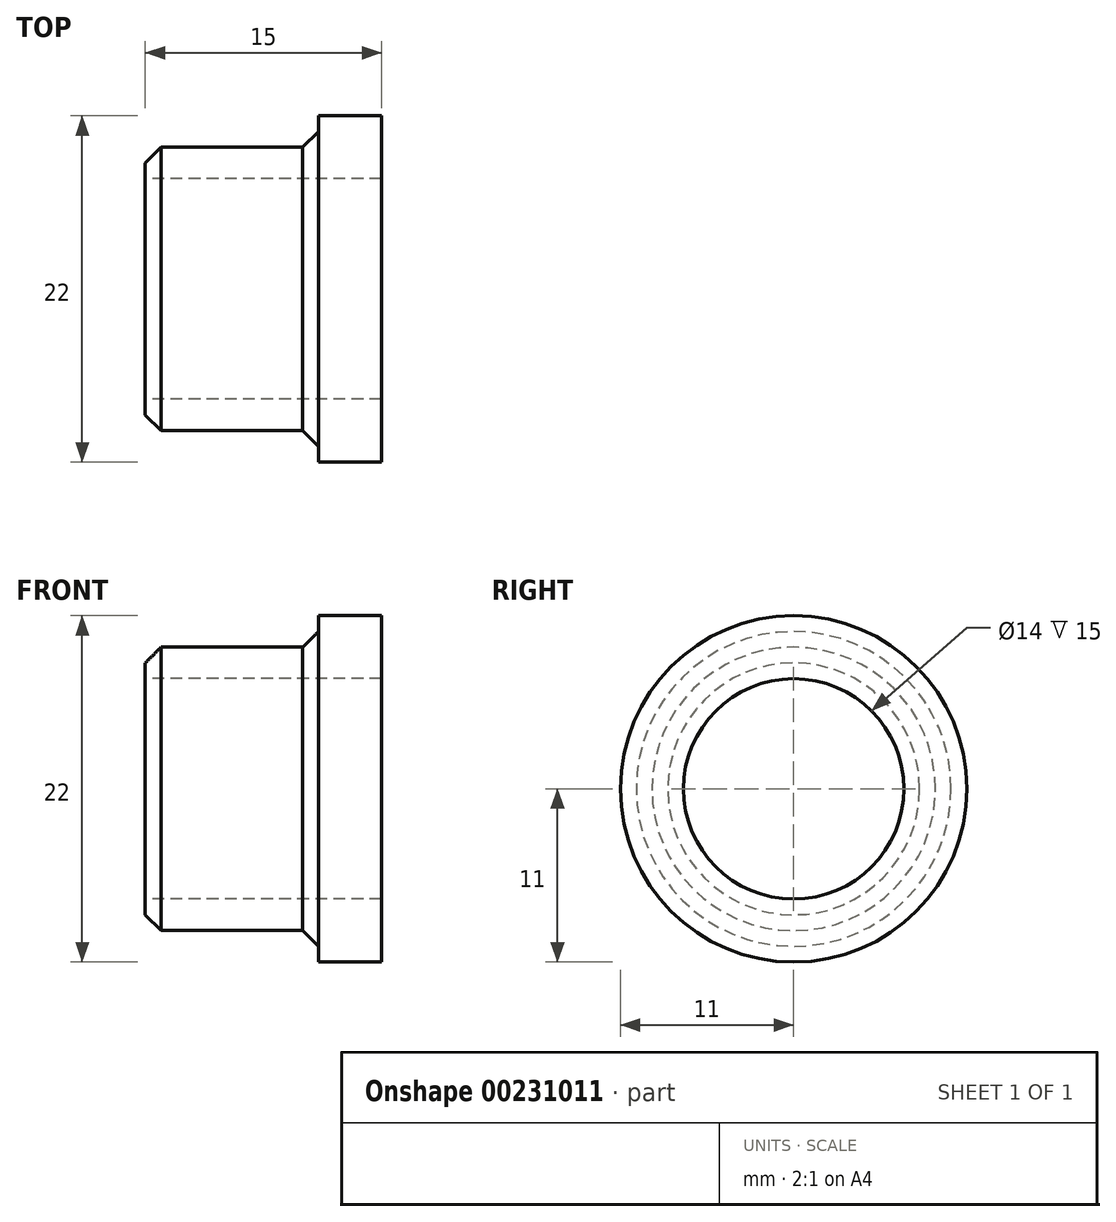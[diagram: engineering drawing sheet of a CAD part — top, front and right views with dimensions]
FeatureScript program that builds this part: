
annotation { "Feature Type Name" : "Feature", "Feature Type Description" : "" }
export const myFeature = defineFeature(function(context is Context, id is Id, definition is map)
    precondition{}
    {
        {
            var Q0;
            Q0=qCreatedBy(makeId("Top.planeOp"),FACE);
            var sketch = newSketch(context, id + "F0", { "sketchPlane" : qUnion([Q0])});
            skLineSegment(sketch, "E0", {"start": v(0, 0) * mm, "end": v(0, 9) * mm});
            skLineSegment(sketch, "E1", {"start": v(0, 9) * mm, "end": v(11, 9) * mm});
            skLineSegment(sketch, "E2", {"start": v(11, 9) * mm, "end": v(11, 11) * mm});
            skLineSegment(sketch, "E3", {"start": v(11, 11) * mm, "end": v(15, 11) * mm});
            skLineSegment(sketch, "E4", {"start": v(15, 11) * mm, "end": v(15, 7) * mm});
            skLineSegment(sketch, "E5", {"start": v(15, 7) * mm, "end": v(0, 7) * mm});
            skLineSegment(sketch, "E6", {"start": v(0, 7) * mm, "end": v(0, 9) * mm});
            skLineSegment(sketch, "E7", {"start": v(-2.5, 0) * mm, "end": v(19.5, 0) * mm, "construction": true});
            skSolve(sketch);
        }
        {
            var Q0;
            Q0=makeQuery(id+"F0.imprint","IMPRINT",FACE,{"disambiguationData":[TD([[makeQuery(id+"F0.imprint","IMPRINT",EDGE,{"derivedFrom":sQuery(id+"F0.wireOp",EDGE,"E1")}),-1.0]])]});
            var Q1;
            Q1=sQuery(id+"F0.wireOp",EDGE,"E7");
            revolve(context, id + "F1", {"entities" : qUnion([Q0]), "axis" : qUnion([Q1]), "revolveType" : RevolveType.FULL});
        }
        {
            var Q0;
            Q0=makeQuery(id+"F1.opRevolve","SWEPT_EDGE",EDGE,{"disambiguationData":[OSD([sQuery(id+"F0.wireOp",EDGE,"E1"),sQuery(id+"F0.wireOp",EDGE,"E6")])]});
            chamfer(context, id + "F2", {"entities" : qUnion([Q0]), "width" : 1 * mm, "tangentPropagation" : true});
        }
    });
